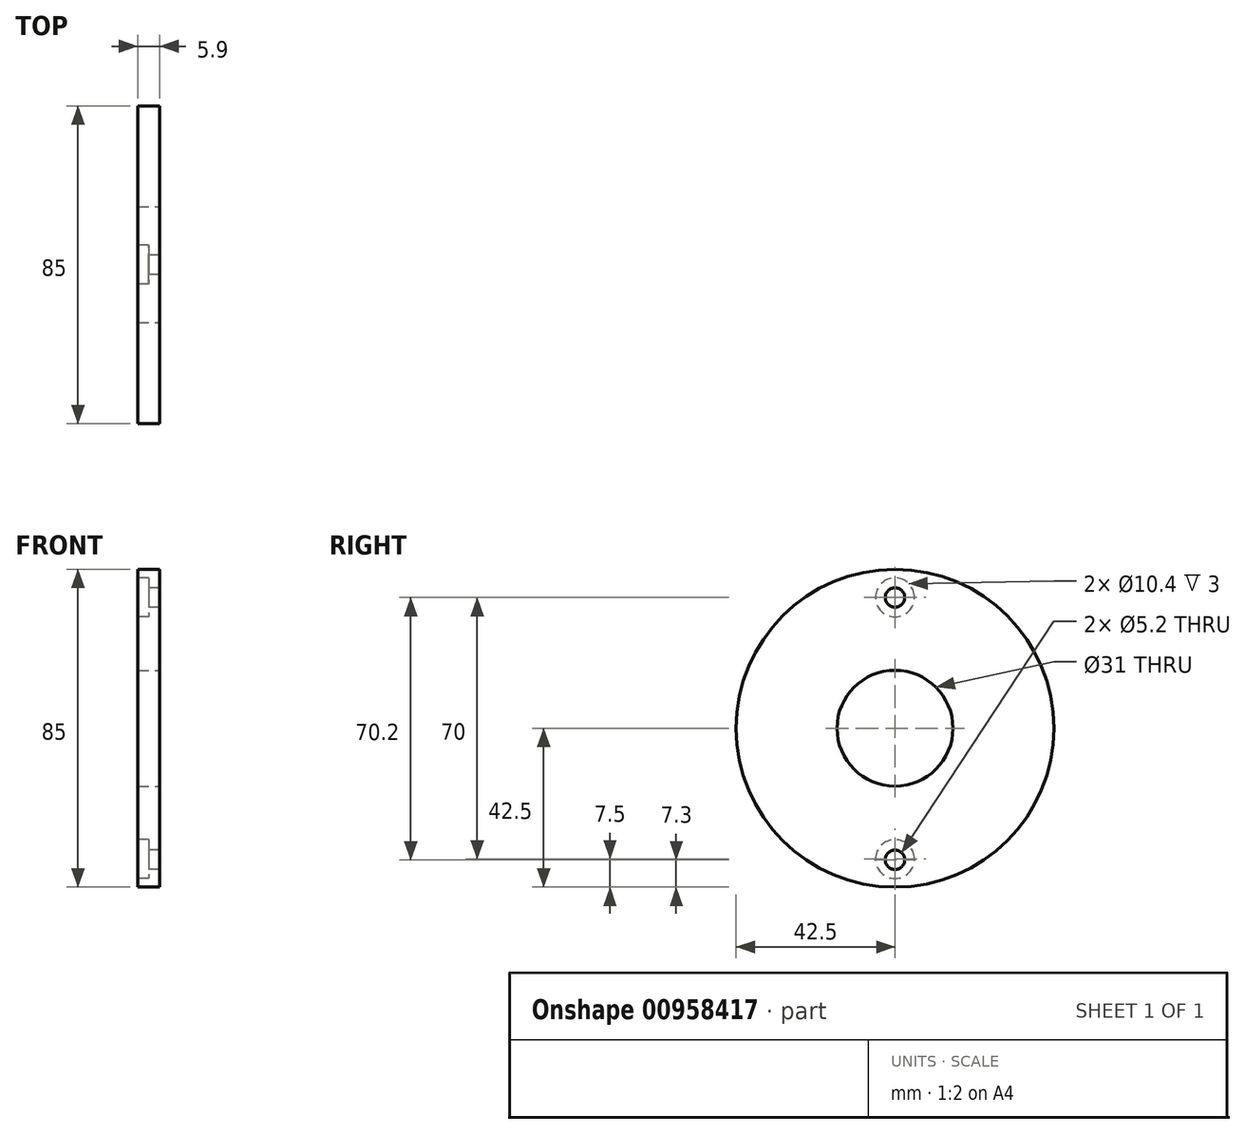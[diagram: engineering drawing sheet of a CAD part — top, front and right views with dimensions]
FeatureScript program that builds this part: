
annotation { "Feature Type Name" : "Feature", "Feature Type Description" : "" }
export const myFeature = defineFeature(function(context is Context, id is Id, definition is map)
    precondition{}
    {
        {
            var Q0;
            Q0=qCreatedBy(makeId("Front.planeOp"),FACE);
            var sketch = newSketch(context, id + "F0", { "sketchPlane" : qUnion([Q0])});
            skLineSegment(sketch, "E0.bottom", {"start": v(8.35, 42.5) * mm, "end": v(2.45, 42.5) * mm});
            skLineSegment(sketch, "E0.top", {"start": v(8.35, 15.5) * mm, "end": v(2.45, 15.5) * mm});
            skLineSegment(sketch, "E0.left", {"start": v(8.35, 42.5) * mm, "end": v(8.35, 15.5) * mm});
            skLineSegment(sketch, "E0.right", {"start": v(2.45, 42.5) * mm, "end": v(2.45, 15.5) * mm});
            skLineSegment(sketch, "E1", {"start": v(0, 0) * mm, "end": v(-9.37, 0) * mm});
            skSolve(sketch);
        }
        {
            var Q0;
            Q0=qSketchRegion(id+"F0",true);
            var Q1;
            Q1=sQuery(id+"F0.wireOp",EDGE,"E1");
            revolve(context, id + "F1", {"surfaceOperationType" : NewSurfaceOperationType.NEW, "entities" : qUnion([Q0]), "axis" : qUnion([Q1]), "revolveType" : RevolveType.FULL});
        }
        {
            var Q0;
            Q0=makeQuery(id+"F1.opRevolve","SWEPT_FACE",FACE,{"disambiguationData":[OSD([sQuery(id+"F0.wireOp",EDGE,"E0.right")])]});
            var sketch = newSketch(context, id + "F2", { "sketchPlane" : qUnion([Q0])});
            skCircle(sketch, "E2", {"center": v(0, 35) * mm, "radius": 5.2 * mm});
            skCircle(sketch, "E3", {"center": v(0, -35) * mm, "radius": 5.2 * mm});
            skSolve(sketch);
        }
        {
            var Q0;
            Q0 = qSketchRegion(id + "F2", true);
            extrude(context, id + "F3", {"entities" : qUnion([Q0]), "operationType" : NewBodyOperationType.REMOVE, "oppositeDirection" : true, "depth" : 3 * mm, "offsetDistance" : 25 * mm});
        }
        {
            var Q0;
            Q0=makeQuery(id+"F3.boolean.opBoolean","COPY",FACE,{"derivedFrom":makeQuery(id+"F3.opExtrude","CAP_FACE",FACE,{"disambiguationData":[OSD([sQuery(id+"F2.wireOp",EDGE,"E2")])],"isStart":false})});
            var sketch = newSketch(context, id + "F4", { "sketchPlane" : qUnion([Q0])});
            skCircle(sketch, "E4", {"center": v(0, 35) * mm, "radius": 2.6 * mm});
            skCircle(sketch, "E5", {"center": v(0, -35.2) * mm, "radius": 2.6 * mm});
            skSolve(sketch);
        }
        {
            var Q0;
            Q0=makeQuery(id+"F4.imprint","IMPRINT",FACE,{"disambiguationData":[TD([[makeQuery(id+"F4.imprint","IMPRINT",EDGE,{"derivedFrom":sQuery(id+"F4.wireOp",EDGE,"E5")}),1.0]])]});
            var Q1;
            Q1=makeQuery(id+"F4.imprint","IMPRINT",FACE,{"disambiguationData":[TD([[makeQuery(id+"F4.imprint","IMPRINT",EDGE,{"derivedFrom":sQuery(id+"F4.wireOp",EDGE,"E4")}),1.0]])]});
            extrude(context, id + "F5", {"entities" : qUnion([Q0, Q1]), "operationType" : NewBodyOperationType.REMOVE, "oppositeDirection" : true, "depth" : 25 * mm, "offsetDistance" : 25 * mm});
        }
    });
